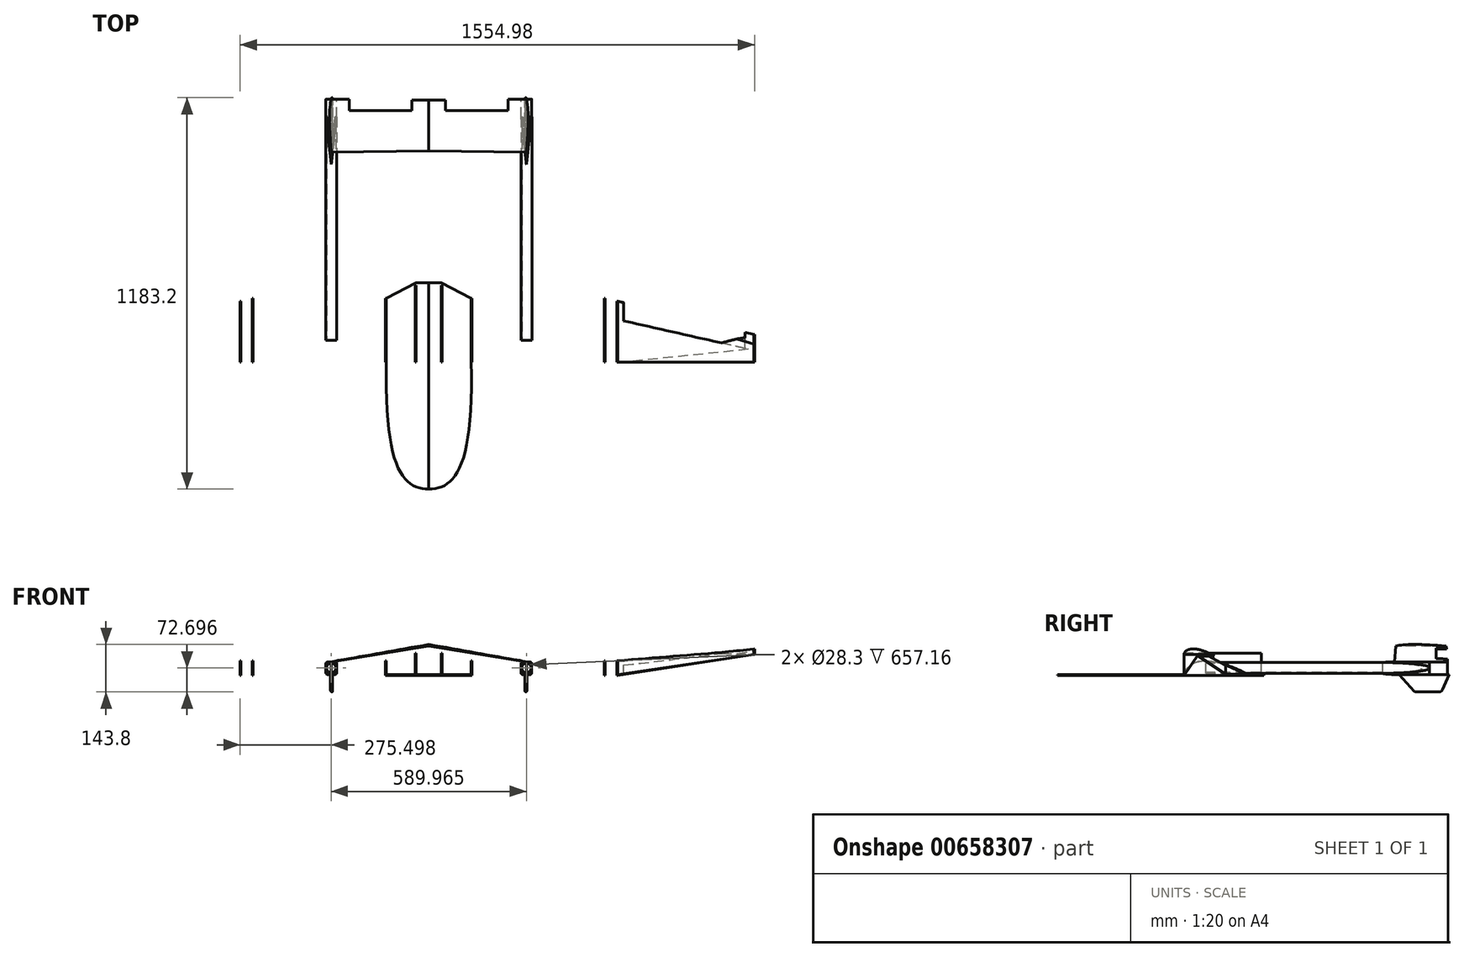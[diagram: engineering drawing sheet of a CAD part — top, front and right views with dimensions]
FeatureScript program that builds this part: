
annotation { "Feature Type Name" : "Feature", "Feature Type Description" : "" }
export const myFeature = defineFeature(function(context is Context, id is Id, definition is map)
    precondition{}
    {
        {
            var Q0;
            Q0=qCreatedBy(makeId("Top.planeOp"),FACE);
            var sketch = newSketch(context, id + "F0", { "sketchPlane" : qUnion([Q0])});
            skLineSegment(sketch, "E0", {"start": v(0, 0) * mm, "end": v(0, -382.94) * mm});
            skFitSpline(sketch, "E1", {"points": [v(0, -382.94) * mm, v(128.36, 0) * mm], "startDerivative": vector(233.61, 0) * mm, "endDerivative": vector(-19.39, 965.68) * mm});
            skLineSegment(sketch, "E2", {"start": v(128.36, 0) * mm, "end": v(1020.01, 0) * mm});
            skLineSegment(sketch, "E3", {"start": v(1020.01, 0) * mm, "end": v(1020.01, 80.94) * mm});
            skLineSegment(sketch, "E4", {"start": v(1020.01, 80.94) * mm, "end": v(531.82, 193.85) * mm});
            skLineSegment(sketch, "E5", {"start": v(531.82, 193.85) * mm, "end": v(128.36, 193.85) * mm});
            skLineSegment(sketch, "E6", {"start": v(0, 240.34) * mm, "end": v(0, 0) * mm});
            skLineSegment(sketch, "E7", {"start": v(128.36, 0) * mm, "end": v(128.36, 193.85) * mm});
            skLineSegment(sketch, "E8", {"start": v(531.82, 193.85) * mm, "end": v(531.82, 0) * mm});
            skLineSegment(sketch, "E9", {"start": v(568.3, 185.41) * mm, "end": v(568.3, 130.1) * mm});
            skLineSegment(sketch, "E10", {"start": v(568.3, 130.1) * mm, "end": v(981.05, 34.63) * mm});
            skLineSegment(sketch, "E11", {"start": v(981.05, 34.63) * mm, "end": v(981.05, 89.95) * mm});
            skLineSegment(sketch, "E12", {"start": v(0, 240.34) * mm, "end": v(38.04, 240.34) * mm});
            skLineSegment(sketch, "E13", {"start": v(38.04, 240.34) * mm, "end": v(128.36, 193.85) * mm});
            skSolve(sketch);
        }
        {
            var Q0;
            Q0=qCreatedBy(makeId("Right.planeOp"),FACE);
            var sketch = newSketch(context, id + "F1", { "sketchPlane" : qUnion([Q0])});
            skFitSpline(sketch, "E14", {"points": [v(-382.75, 0) * mm, v(0, 95.17) * mm], "startDerivative": vector(82.74, 188.65) * mm, "endDerivative": vector(471.18, 30.82) * mm});
            skLineSegment(sketch, "E15", {"start": v(-382.75, 0) * mm, "end": v(240.8, 0) * mm});
            skLineSegment(sketch, "E16", {"start": v(240.8, 0) * mm, "end": v(240.8, 95.17) * mm});
            skLineSegment(sketch, "E17", {"start": v(240.8, 95.17) * mm, "end": v(0, 95.17) * mm});
            skSolve(sketch);
        }
        {
            var Q0;
            Q0=sQuery(id+"F0.wireOp",EDGE,"E1");
            var Q1;
            Q1=sQuery(id+"F1.wireOp",EDGE,"E14");
            loft(context, id + "F2", {"bodyType" : ToolBodyType.SURFACE, "wireProfilesArray" : [{ "wireProfileEntities" : qUnion([Q0]) }, { "wireProfileEntities" : qUnion([Q1]) }]});
        }
        {
            var Q0;
            Q0=makeQuery(id+"F0.imprint","IMPRINT",FACE,{"disambiguationData":[TD([[makeQuery(id+"F0.imprint","IMPRINT",EDGE,{"derivedFrom":sQuery(id+"F0.wireOp",EDGE,"E0")}),1.0]])]});
            extrude(context, id + "F3", {"entities" : qUnion([Q0]), "oppositeDirection" : true, "depth" : 2.54 * mm, "offsetDistance" : 25.4 * mm});
        }
        {
            var Q0;
            Q0=makeQuery(id+"F3.opExtrude","SWEPT_FACE",FACE,{"disambiguationData":[OSD([sQuery(id+"F0.wireOp",EDGE,"E7")])]});
            var sketch = newSketch(context, id + "F4", { "sketchPlane" : qUnion([Q0])});
            skFitSpline(sketch, "E18", {"points": [v(0, 0) * mm, v(193.85, 0) * mm], "startDerivative": vector(91.66, 269.25) * mm, "endDerivative": vector(55.9, -26.92) * mm});
            skLineSegment(sketch, "E19", {"start": v(0, 0) * mm, "end": v(0, -2.54) * mm});
            skLineSegment(sketch, "E20", {"start": v(0, -2.54) * mm, "end": v(193.85, -2.54) * mm});
            skLineSegment(sketch, "E21", {"start": v(193.85, -2.54) * mm, "end": v(193.85, 0) * mm});
            skSolve(sketch);
        }
        {
            var Q0;
            Q0 = qSketchRegion(id + "F4", true);
            extrude(context, id + "F5", {"entities" : qUnion([Q0]), "operationType" : NewBodyOperationType.ADD, "depth" : 2.54 * mm, "offsetDistance" : 25.4 * mm});
        }
        {
            var Q0;
            Q0=qCreatedBy(makeId("Right.planeOp"),FACE);
            cPlane(context, id + "F6", {"entities" : qUnion([Q0]), "cplaneType" : CPlaneType.OFFSET, "offset" : 40.64 * mm, "width" : 152.4 * mm, "height" : 152.4 * mm});
        }
        {
            var Q0;
            Q0=qCreatedBy(id+"F6.planeOp",FACE);
            var sketch = newSketch(context, id + "F7", { "sketchPlane" : qUnion([Q0])});
            skLineSegment(sketch, "E22", {"start": v(0, 65.06) * mm, "end": v(0, 0) * mm});
            skLineSegment(sketch, "E23", {"start": v(0, 0) * mm, "end": v(233.41, 0) * mm});
            skLineSegment(sketch, "E24", {"start": v(233.41, 0) * mm, "end": v(233.41, 65.06) * mm});
            skLineSegment(sketch, "E25", {"start": v(233.41, 65.06) * mm, "end": v(0, 65.06) * mm});
            skSolve(sketch);
        }
        {
            var Q0;
            Q0 = qSketchRegion(id + "F7", true);
            extrude(context, id + "F8", {"entities" : qUnion([Q0]), "operationType" : NewBodyOperationType.ADD, "oppositeDirection" : true, "depth" : 2.54 * mm, "offsetDistance" : 25.4 * mm});
        }
        {
            var Q0;
            Q0=makeQuery(id+"F8.opExtrude","CAP_EDGE",EDGE,{"disambiguationData":[OSD([sQuery(id+"F7.wireOp",EDGE,"E25")])],"isStart":true});
            var Q1;
            Q1=sQuery(id+"F1.wireOp",EDGE,"E17");
            loft(context, id + "F9", {"bodyType" : ToolBodyType.SURFACE, "wireProfilesArray" : [{ "wireProfileEntities" : qUnion([Q0]) }, { "wireProfileEntities" : qUnion([Q1]) }]});
        }
        {
            var Q0;
            Q0=makeQuery(id+"F9.opLoft","SWEPT_BODY",BODY,{"disambiguationData":[OSD([sQuery(id+"F1.wireOp",EDGE,"E17"),sQuery(id+"F7.wireOp",EDGE,"E25")])]});
            var Q1;
            Q1=makeQuery(id+"F9.opLoft","MID_CAP_EDGE",EDGE,{"disambiguationData":[OSD([sQuery(id+"F7.wireOp",EDGE,"E22"),sQuery(id+"F7.wireOp",EDGE,"E24"),sQuery(id+"F7.wireOp",EDGE,"E25")])],"capPos":0.0});
            var Q2;
            Q2=makeQuery(id+"F5.opExtrude","CAP_EDGE",EDGE,{"disambiguationData":[OSD([sQuery(id+"F4.wireOp",EDGE,"E18")])],"isStart":true});
            loft(context, id + "F10", {"bodyType" : ToolBodyType.SURFACE, "sheetProfilesArray" : [{ "sheetProfileEntities" : qUnion([Q0]) }], "wireProfilesArray" : [{ "wireProfileEntities" : qUnion([Q1]) }, { "wireProfileEntities" : qUnion([Q2]) }]});
        }
        {
            var Q0;
            Q0=qCreatedBy(makeId("Right.planeOp"),FACE);
            cPlane(context, id + "F11", {"entities" : qUnion([Q0]), "cplaneType" : CPlaneType.OFFSET, "offset" : 530.86 * mm, "width" : 152.4 * mm, "height" : 152.4 * mm});
        }
        {
            var Q0;
            Q0=qCreatedBy(id+"F11.planeOp",FACE);
            var sketch = newSketch(context, id + "F12", { "sketchPlane" : qUnion([Q0])});
            skFitSpline(sketch, "E26", {"points": [v(0, 0) * mm, v(193.85, 0) * mm], "startDerivative": vector(87.77, 268.75) * mm, "endDerivative": vector(39.83, -20.5) * mm});
            skLineSegment(sketch, "E27", {"start": v(193.85, 0) * mm, "end": v(193.85, -2.56) * mm});
            skLineSegment(sketch, "E28", {"start": v(0, 0) * mm, "end": v(0, -2.54) * mm});
            skLineSegment(sketch, "E29", {"start": v(0, -2.54) * mm, "end": v(193.85, -2.56) * mm});
            skSolve(sketch);
        }
        {
            var Q0;
            Q0 = qSketchRegion(id + "F12", true);
            extrude(context, id + "F13", {"entities" : qUnion([Q0]), "depth" : 2.54 * mm, "offsetDistance" : 25.4 * mm});
        }
        {
            var Q0;
            Q0=makeQuery(id+"F5.opExtrude","CAP_EDGE",EDGE,{"disambiguationData":[OSD([sQuery(id+"F4.wireOp",EDGE,"E18")])],"isStart":false});
            var Q1;
            Q1=makeQuery(id+"F13.opExtrude","CAP_EDGE",EDGE,{"disambiguationData":[OSD([sQuery(id+"F12.wireOp",EDGE,"E26")])],"isStart":true});
            loft(context, id + "F14", {"bodyType" : ToolBodyType.SURFACE, "wireProfilesArray" : [{ "wireProfileEntities" : qUnion([Q0]) }, { "wireProfileEntities" : qUnion([Q1]) }]});
        }
        {
            var Q0;
            Q0=sQuery(id+"F0.wireOp",EDGE,"E7");
            var Q1;
            Q1=makeQuery(id+"F13.opExtrude","CAP_EDGE",EDGE,{"disambiguationData":[OSD([sQuery(id+"F12.wireOp",EDGE,"E29")])],"isStart":true});
            loft(context, id + "F15", {"bodyType" : ToolBodyType.SURFACE, "wireProfilesArray" : [{ "wireProfileEntities" : qUnion([Q0]) }, { "wireProfileEntities" : qUnion([Q1]) }]});
        }
        {
            var Q0;
            Q0=qCreatedBy(id+"F11.planeOp",FACE);
            cPlane(context, id + "F16", {"entities" : qUnion([Q0]), "cplaneType" : CPlaneType.OFFSET, "offset" : 37.08 * mm, "width" : 152.4 * mm, "height" : 152.4 * mm});
        }
        {
            var Q0;
            Q0=qCreatedBy(id+"F16.planeOp",FACE);
            var sketch = newSketch(context, id + "F17", { "sketchPlane" : qUnion([Q0])});
            skFitSpline(sketch, "E30", {"points": [v(0, 0) * mm, v(185.26, 0) * mm], "startDerivative": vector(98.18, 281.16) * mm, "endDerivative": vector(14.13, 0) * mm});
            skLineSegment(sketch, "E31", {"start": v(0, 0) * mm, "end": v(0, -2.42) * mm});
            skLineSegment(sketch, "E32", {"start": v(0, -2.42) * mm, "end": v(185.14, -2.42) * mm});
            skLineSegment(sketch, "E33", {"start": v(185.14, -2.42) * mm, "end": v(185.26, 0) * mm});
            skLineSegment(sketch, "E34", {"start": v(131.84, -2.42) * mm, "end": v(131.84, 25.26) * mm});
            skSolve(sketch);
        }
        {
            var Q0;
            Q0 = qSketchRegion(id + "F17", true);
            extrude(context, id + "F18", {"entities" : qUnion([Q0]), "depth" : 2.54 * mm, "offsetDistance" : 25.4 * mm});
        }
        {
            var Q0;
            Q0=makeQuery(id+"F13.opExtrude","CAP_FACE",FACE,{"disambiguationData":[OSD([sQuery(id+"F12.wireOp",EDGE,"E26"),sQuery(id+"F12.wireOp",EDGE,"E27"),sQuery(id+"F12.wireOp",EDGE,"E28"),sQuery(id+"F12.wireOp",EDGE,"E29")])],"isStart":false});
            var Q1;
            Q1=makeQuery(id+"F13.opExtrude","CAP_EDGE",EDGE,{"disambiguationData":[OSD([sQuery(id+"F12.wireOp",EDGE,"E26")])],"isStart":false});
            var Q2;
            Q2=makeQuery(id+"F18.opExtrude","CAP_EDGE",EDGE,{"disambiguationData":[OSD([sQuery(id+"F17.wireOp",EDGE,"E30")])],"isStart":true});
            loft(context, id + "F19", {"bodyType" : ToolBodyType.SURFACE, "sheetProfilesArray" : [{ "sheetProfileEntities" : qUnion([Q0]) }], "wireProfilesArray" : [{ "wireProfileEntities" : qUnion([Q1]) }, { "wireProfileEntities" : qUnion([Q2]) }]});
        }
        {
            var Q0;
            Q0=makeQuery(id+"F18.opExtrude","CAP_EDGE",EDGE,{"disambiguationData":[OSD([sQuery(id+"F17.wireOp",EDGE,"E32")])],"isStart":true});
            var Q1;
            Q1=makeQuery(id+"F13.opExtrude","CAP_EDGE",EDGE,{"disambiguationData":[OSD([sQuery(id+"F12.wireOp",EDGE,"E29")])],"isStart":false});
            loft(context, id + "F20", {"bodyType" : ToolBodyType.SURFACE, "wireProfilesArray" : [{ "wireProfileEntities" : qUnion([Q0]) }, { "wireProfileEntities" : qUnion([Q1]) }]});
        }
        {
            var Q0;
            Q0=qCreatedBy(id+"F16.planeOp",FACE);
            cPlane(context, id + "F21", {"entities" : qUnion([Q0]), "cplaneType" : CPlaneType.OFFSET, "offset" : 414.02 * mm, "width" : 152.4 * mm, "height" : 152.4 * mm});
        }
        {
            var Q0;
            Q0=qCreatedBy(id+"F21.planeOp",FACE);
            var sketch = newSketch(context, id + "F22", { "sketchPlane" : qUnion([Q0])});
            skLineSegment(sketch, "E35", {"start": v(0, 60.1) * mm, "end": v(84.44, 60.1) * mm});
            skLineSegment(sketch, "E36", {"start": v(27.71, 60.1) * mm, "end": v(27.71, 77.24) * mm});
            skFitSpline(sketch, "E37", {"points": [v(0, 60.1) * mm, v(27.71, 77.24) * mm, v(84.44, 60.1) * mm], "startDerivative": vector(0, 93.67) * mm, "endDerivative": vector(108.46, -49.98) * mm});
            skSolve(sketch);
        }
        {
            var Q0;
            Q0 = qSketchRegion(id + "F22", true);
            extrude(context, id + "F23", {"entities" : qUnion([Q0]), "depth" : 2.54 * mm, "offsetDistance" : 25.4 * mm});
        }
        {
            var Q0;
            Q0=makeQuery(id+"F18.opExtrude","CAP_FACE",FACE,{"disambiguationData":[OSD([sQuery(id+"F17.wireOp",EDGE,"E30"),sQuery(id+"F17.wireOp",EDGE,"E31"),sQuery(id+"F17.wireOp",EDGE,"E32"),sQuery(id+"F17.wireOp",EDGE,"E33")])],"isStart":false});
            var Q1;
            Q1=makeQuery(id+"F23.opExtrude","CAP_FACE",FACE,{"disambiguationData":[OSD([sQuery(id+"F22.wireOp",EDGE,"c30c6b66-d443-4e39-8451-170bddd20a5f"),sQuery(id+"F22.wireOp",EDGE,"S6skx1oO-r8w3-M7RH-89HN-Rbgwb9d3iRie"),sQuery(id+"F22.wireOp",EDGE,"E35"),sQuery(id+"F22.wireOp",EDGE,"XofBSCwt-zFux-jAat-FpLT-tnajAGSUlYNw")])],"isStart":true});
            loft(context, id + "F24", {"sheetProfilesArray" : [{ "sheetProfileEntities" : qUnion([Q0]) }, { "sheetProfileEntities" : qUnion([Q1]) }]});
        }
        {
            var Q0;
            Q0=qCreatedBy(makeId("Top.planeOp"),FACE);
            var sketch = newSketch(context, id + "F25", { "sketchPlane" : qUnion([Q0])});
            skLineSegment(sketch, "E38", {"start": v(589.31, 183.72) * mm, "end": v(589.31, 125.4) * mm});
            skLineSegment(sketch, "E39", {"start": v(589.31, 125.4) * mm, "end": v(956.1, 42.53) * mm});
            skLineSegment(sketch, "E40", {"start": v(956.1, 42.53) * mm, "end": v(956.1, 97.78) * mm});
            skLineSegment(sketch, "E41", {"start": v(956.1, 97.78) * mm, "end": v(589.31, 183.72) * mm});
            skSolve(sketch);
        }
        {
            var Q0;
            Q0 = qSketchRegion(id + "F25", true);
            extrude(context, id + "F26", {"entities" : qUnion([Q0]), "operationType" : NewBodyOperationType.REMOVE, "oppositeDirection" : true, "depth" : 25.4 * mm, "offsetDistance" : 25.4 * mm, "hasSecondDirection" : true, "secondDirectionOppositeDirection" : false, "secondDirectionDepth" : 63.5 * mm});
        }
        {
            var Q0;
            Q0=qCreatedBy(makeId("Front.planeOp"),FACE);
            cPlane(context, id + "F27", {"entities" : qUnion([Q0]), "cplaneType" : CPlaneType.OFFSET, "offset" : 66.04 * mm, "oppositeDirection" : true, "width" : 152.4 * mm, "height" : 152.4 * mm});
        }
        {
            var Q0;
            Q0=qCreatedBy(id+"F27.planeOp",FACE);
            var sketch = newSketch(context, id + "F28", { "sketchPlane" : qUnion([Q0])});
            skCircle(sketch, "E42", {"center": v(294.98, 19.94) * mm, "radius": 16.32 * mm});
            skCircle(sketch, "E43", {"center": v(294.98, 19.94) * mm, "radius": 14.15 * mm});
            skSolve(sketch);
        }
        {
            var Q0;
            Q0 = qSketchRegion(id + "F28", true);
            extrude(context, id + "F29", {"entities" : qUnion([Q0]), "operationType" : NewBodyOperationType.ADD, "oppositeDirection" : true, "depth" : 675.64 * mm, "offsetDistance" : 25.4 * mm});
        }
        {
            var Q0;
            Q0=qCreatedBy(makeId("Top.planeOp"),FACE);
            var sketch = newSketch(context, id + "F30", { "sketchPlane" : qUnion([Q0])});
            skLineSegment(sketch, "E44", {"start": v(294.86, 741.49) * mm, "end": v(294.86, 598.34) * mm});
            skFitSpline(sketch, "E45", {"points": [v(294.86, 598.34) * mm, v(311.17, 741.68) * mm], "startDerivative": vector(15.62, 145.99) * mm, "endDerivative": vector(15.62, 145.99) * mm});
            skLineSegment(sketch, "E46", {"start": v(311.17, 741.68) * mm, "end": v(311.17, 795.98) * mm});
            skLineSegment(sketch, "E47", {"start": v(311.17, 795.98) * mm, "end": v(294.86, 795.98) * mm});
            skLineSegment(sketch, "E48", {"start": v(294.86, 795.98) * mm, "end": v(294.86, 741.49) * mm});
            skLineSegment(sketch, "E49.MirrorCS", {"start": v(278.55, 795.98) * mm, "end": v(294.86, 795.98) * mm});
            skLineSegment(sketch, "E50.MirrorCS", {"start": v(278.55, 741.68) * mm, "end": v(278.55, 795.98) * mm});
            skFitSpline(sketch, "E51.MirrorCS", {"points": [v(294.86, 598.34) * mm, v(278.55, 741.68) * mm], "startDerivative": vector(-15.62, 145.99) * mm, "endDerivative": vector(-15.62, 145.99) * mm});
            skSolve(sketch);
        }
        {
            var Q0;
            Q0 = qSketchRegion(id + "F30", true);
            extrude(context, id + "F31", {"entities" : qUnion([Q0]), "operationType" : NewBodyOperationType.ADD, "depth" : 37.85 * mm, "offsetDistance" : 25.4 * mm});
        }
        {
            var Q0;
            Q0=makeQuery(id+"F31.opExtrude","CAP_EDGE",EDGE,{"disambiguationData":[OSD([sQuery(id+"F30.wireOp",EDGE,"E45")])],"isStart":false});
            var Q1;
            Q1=makeQuery(id+"F31.opExtrude","CAP_EDGE",EDGE,{"disambiguationData":[OSD([sQuery(id+"F30.wireOp",EDGE,"E46")])],"isStart":false});
            var Q2;
            Q2=makeQuery(id+"F31.opExtrude","CAP_EDGE",EDGE,{"disambiguationData":[OSD([sQuery(id+"F30.wireOp",EDGE,"E45")])],"isStart":true});
            var Q3;
            Q3=makeQuery(id+"F31.opExtrude","CAP_EDGE",EDGE,{"disambiguationData":[OSD([sQuery(id+"F30.wireOp",EDGE,"E46")])],"isStart":true});
            var Q4;
            Q4=makeQuery(id+"F31.opExtrude","CAP_EDGE",EDGE,{"disambiguationData":[OSD([sQuery(id+"F30.wireOp",EDGE,"E50.MirrorCS")])],"isStart":false});
            var Q5;
            Q5=makeQuery(id+"F31.opExtrude","CAP_EDGE",EDGE,{"disambiguationData":[OSD([sQuery(id+"F30.wireOp",EDGE,"E51.MirrorCS")])],"isStart":false});
            var Q6;
            Q6=makeQuery(id+"F31.opExtrude","CAP_EDGE",EDGE,{"disambiguationData":[OSD([sQuery(id+"F30.wireOp",EDGE,"E50.MirrorCS")])],"isStart":true});
            var Q7;
            Q7=makeQuery(id+"F31.opExtrude","CAP_EDGE",EDGE,{"disambiguationData":[OSD([sQuery(id+"F30.wireOp",EDGE,"E51.MirrorCS")])],"isStart":true});
            fillet(context, id + "F32", {"entities" : qUnion([Q0, Q1, Q2, Q3, Q4, Q5, Q6, Q7]), "radius" : 5.08 * mm, "tangentPropagation" : true, "allowEdgeOverflow" : false});
        }
        {
            var Q0;
            Q0=sQuery(id+"F0.wireOp",EDGE,"E2");
            var Q1;
            Q1=makeQuery(id+"F15.opLoft","SWEPT_EDGE",EDGE,{"disambiguationData":[OSD([sQuery(id+"F0.wireOp",VERTEX,"E7.start"),sQuery(id+"F12.wireOp",EDGE,"E28"),sQuery(id+"F12.wireOp",EDGE,"E29")])]});
            loft(context, id + "F33", {"bodyType" : ToolBodyType.SURFACE, "wireProfilesArray" : [{ "wireProfileEntities" : qUnion([Q0]) }, { "wireProfileEntities" : qUnion([Q1]) }]});
        }
        {
            var Q0;
            Q0=makeQuery(id+"F10.opLoft","SWEPT_EDGE",EDGE,{"disambiguationData":[OSD([sQuery(id+"F0.wireOp",EDGE,"E5"),sQuery(id+"F0.wireOp",EDGE,"E7"),sQuery(id+"F0.wireOp",EDGE,"E13"),sQuery(id+"F4.wireOp",EDGE,"E18"),sQuery(id+"F4.wireOp",EDGE,"E21"),sQuery(id+"F7.wireOp",EDGE,"E24"),sQuery(id+"F7.wireOp",EDGE,"E25")])]});
            var Q1;
            Q1=sQuery(id+"F0.wireOp",EDGE,"E13");
            loft(context, id + "F34", {"bodyType" : ToolBodyType.SURFACE, "wireProfilesArray" : [{ "wireProfileEntities" : qUnion([Q0]) }, { "wireProfileEntities" : qUnion([Q1]) }]});
        }
        {
            var Q0;
            Q0=qCreatedBy(makeId("Right.planeOp"),FACE);
            cPlane(context, id + "F35", {"entities" : qUnion([Q0]), "cplaneType" : CPlaneType.OFFSET, "offset" : 293.88 * mm, "width" : 152.4 * mm, "height" : 152.4 * mm});
        }
        {
            var Q0;
            Q0=qCreatedBy(id+"F35.planeOp",FACE);
            var sketch = newSketch(context, id + "F36", { "sketchPlane" : qUnion([Q0])});
            skLineSegment(sketch, "E52", {"start": v(800.26, 0) * mm, "end": v(780.86, -45.8) * mm});
            skLineSegment(sketch, "E53", {"start": v(770.33, -52.76) * mm, "end": v(700.76, -52.76) * mm});
            skLineSegment(sketch, "E54", {"start": v(696.08, -50.71) * mm, "end": v(649.46, 0) * mm});
            skLineSegment(sketch, "E55", {"start": v(649.46, 0) * mm, "end": v(800.26, 0) * mm});
            skPoint(sketch, "E56.visualSharp", {"position": v(697.97, -52.76) * mm});
            skArc(sketch, "E56.filletArc", {"start": v(696.08, -50.71) * mm, "mid": v(698.2, -52.23) * mm, "end": v(700.76, -52.76) * mm});
            skPoint(sketch, "E57.visualSharp", {"position": v(777.9, -52.76) * mm});
            skArc(sketch, "E57.filletArc", {"start": v(770.33, -52.76) * mm, "mid": v(776.65, -50.86) * mm, "end": v(780.86, -45.8) * mm});
            skSolve(sketch);
        }
        {
            var Q0;
            Q0 = qSketchRegion(id + "F36", true);
            extrude(context, id + "F37", {"entities" : qUnion([Q0]), "operationType" : NewBodyOperationType.ADD, "endBound" : BoundingType.SYMMETRIC, "depth" : 6.35 * mm, "offsetDistance" : 25.4 * mm});
        }
        {
            var Q0;
            Q0=makeQuery(id+"F37.opExtrude","CAP_EDGE",EDGE,{"disambiguationData":[OSD([sQuery(id+"F36.wireOp",EDGE,"E54")])],"isStart":false});
            fillet(context, id + "F38", {"entities" : qUnion([Q0]), "radius" : 5.08 * mm, "tangentPropagation" : true, "allowEdgeOverflow" : false});
        }
        {
            var Q0;
            Q0=makeQuery(id+"F37.opExtrude","CAP_EDGE",EDGE,{"disambiguationData":[OSD([sQuery(id+"F36.wireOp",EDGE,"E54")])],"isStart":true});
            fillet(context, id + "F39", {"entities" : qUnion([Q0]), "radius" : 5.08 * mm, "tangentPropagation" : true, "allowEdgeOverflow" : false});
        }
        {
            var Q0;
            Q0=makeQuery(id+"F31.opExtrude","CAP_FACE",FACE,{"disambiguationData":[OSD([sQuery(id+"F30.wireOp",EDGE,"E45"),sQuery(id+"F30.wireOp",EDGE,"E46"),sQuery(id+"F30.wireOp",EDGE,"E47"),sQuery(id+"F30.wireOp",EDGE,"E49.MirrorCS"),sQuery(id+"F30.wireOp",EDGE,"E50.MirrorCS"),sQuery(id+"F30.wireOp",EDGE,"E51.MirrorCS")])],"isStart":false});
            var sketch = newSketch(context, id + "F40", { "sketchPlane" : qUnion([Q0])});
            skLineSegment(sketch, "E58", {"start": v(294.88, 635.6) * mm, "end": v(294.88, 795.98) * mm});
            skFitSpline(sketch, "E59", {"points": [v(294.88, 635.6) * mm, v(294.88, 795.98) * mm], "startDerivative": vector(5.18, 56.04) * mm, "endDerivative": vector(-33.62, 106.5) * mm});
            skSolve(sketch);
        }
        {
            var Q0;
            Q0=makeQuery(id+"F40.imprint","IMPRINT",FACE,{"disambiguationData":[TD([[makeQuery(id+"F40.imprint","IMPRINT",EDGE,{"derivedFrom":sQuery(id+"F40.wireOp",EDGE,"E58")}),-1.0]])]});
            var sketch = newSketch(context, id + "F41", { "sketchPlane" : qUnion([Q0])});
            skSolve(sketch);
        }
        {
            var Q0;
            Q0=qCreatedBy(makeId("Right.planeOp"),FACE);
            var sketch = newSketch(context, id + "F42", { "sketchPlane" : qUnion([Q0])});
            skLineSegment(sketch, "E60", {"start": v(792.55, 85.65) * mm, "end": v(639.4, 85.65) * mm});
            skFitSpline(sketch, "E61", {"points": [v(792.55, 85.65) * mm, v(639.4, 85.65) * mm], "startDerivative": vector(-56.04, 5.21) * mm, "endDerivative": vector(-106.5, -33.62) * mm});
            skSolve(sketch);
        }
        {
            var Q1;
            Q1=makeQuery(id+"F42.imprint","IMPRINT",FACE,{"disambiguationData":[TD([[makeQuery(id+"F42.imprint","IMPRINT",EDGE,{"derivedFrom":sQuery(id+"F42.wireOp",EDGE,"E60")}),-1.0]])]});
            var Q2;
            Q2=makeQuery(id+"F41.imprint","IMPRINT",FACE,{"disambiguationData":[TD([[makeQuery(id+"F41.imprint","IMPRINT",EDGE,{"derivedFrom":makeQuery(id+"F40.imprint","IMPRINT",EDGE,{"derivedFrom":sQuery(id+"F40.wireOp",EDGE,"E58")})}),-1.0]])]});
            loft(context, id + "F43", {"operationType" : NewBodyOperationType.ADD, "sheetProfilesArray" : [{ "sheetProfileEntities" : qUnion([Q1]) }, { "sheetProfileEntities" : qUnion([Q2]) }]});
        }
        {
            var Q0;
            Q0=qCreatedBy(makeId("Top.planeOp"),FACE);
            var sketch = newSketch(context, id + "F44", { "sketchPlane" : qUnion([Q0])});
            skLineSegment(sketch, "E62.bottom", {"start": v(239.97, 822.85) * mm, "end": v(50.83, 822.85) * mm});
            skLineSegment(sketch, "E62.top", {"start": v(239.97, 761.32) * mm, "end": v(50.83, 761.32) * mm});
            skLineSegment(sketch, "E62.left", {"start": v(239.97, 822.85) * mm, "end": v(239.97, 761.32) * mm});
            skLineSegment(sketch, "E62.right", {"start": v(50.83, 822.85) * mm, "end": v(50.83, 761.32) * mm});
            skSolve(sketch);
        }
        {
            var Q0;
            Q0=makeQuery(id+"F44.imprint","IMPRINT",FACE,{"disambiguationData":[TD([[makeQuery(id+"F44.imprint","IMPRINT",EDGE,{"derivedFrom":sQuery(id+"F44.wireOp",EDGE,"E62.bottom")}),1.0]])]});
            extrude(context, id + "F45", {"entities" : qUnion([Q0]), "operationType" : NewBodyOperationType.REMOVE, "depth" : 335.28 * mm, "offsetDistance" : 25.4 * mm});
        }
        {
            var Q0;
            Q0=makeQuery(id+"F2.opLoft","SWEPT_BODY",BODY,{"disambiguationData":[OSD([sQuery(id+"F0.wireOp",EDGE,"E1"),sQuery(id+"F1.wireOp",EDGE,"E14")])]});
            var Q1;
            Q1=makeQuery(id+"F14.opLoft","SWEPT_BODY",BODY,{"disambiguationData":[OSD([sQuery(id+"F4.wireOp",EDGE,"E18"),sQuery(id+"F12.wireOp",EDGE,"E26")])]});
            var Q2;
            Q2=makeQuery(id+"F18.opExtrude","SWEPT_BODY",BODY,{"disambiguationData":[OSD([sQuery(id+"F17.wireOp",EDGE,"E30"),sQuery(id+"F17.wireOp",EDGE,"E31"),sQuery(id+"F17.wireOp",EDGE,"E32"),sQuery(id+"F17.wireOp",EDGE,"E33")])]});
            var Q3;
            Q3=makeQuery(id+"F29.opExtrude","SWEPT_BODY",BODY,{"disambiguationData":[OSD([sQuery(id+"F28.wireOp",EDGE,"E42"),sQuery(id+"F28.wireOp",EDGE,"E43")])]});
            var Q4;
            Q4=makeQuery(id+"F3.opExtrude","SWEPT_BODY",BODY,{"disambiguationData":[OSD([sQuery(id+"F0.wireOp",EDGE,"E0"),sQuery(id+"F0.wireOp",EDGE,"E1"),sQuery(id+"F0.wireOp",EDGE,"E6"),sQuery(id+"F0.wireOp",EDGE,"E7"),sQuery(id+"F0.wireOp",EDGE,"E12"),sQuery(id+"F0.wireOp",EDGE,"E13")])]});
            var Q5;
            Q5=makeQuery(id+"F15.opLoft","SWEPT_BODY",BODY,{"disambiguationData":[OSD([sQuery(id+"F0.wireOp",EDGE,"E7"),sQuery(id+"F12.wireOp",EDGE,"E29")])]});
            var Q6;
            Q6=makeQuery(id+"F19.opLoft","SWEPT_BODY",BODY,{"disambiguationData":[OSD([sQuery(id+"F12.wireOp",EDGE,"E26"),sQuery(id+"F17.wireOp",EDGE,"E30")])]});
            var Q7;
            Q7=makeQuery(id+"F33.opLoft","SWEPT_BODY",BODY,{"disambiguationData":[OSD([sQuery(id+"F0.wireOp",VERTEX,"E7.start"),sQuery(id+"F0.wireOp",EDGE,"E2"),sQuery(id+"F12.wireOp",EDGE,"E28"),sQuery(id+"F12.wireOp",EDGE,"E29")])]});
            var Q8;
            Q8=makeQuery(id+"F9.opLoft","SWEPT_BODY",BODY,{"disambiguationData":[OSD([sQuery(id+"F1.wireOp",EDGE,"E17"),sQuery(id+"F7.wireOp",EDGE,"E25")])]});
            var Q9;
            Q9=makeQuery(id+"F13.opExtrude","SWEPT_BODY",BODY,{"disambiguationData":[OSD([sQuery(id+"F12.wireOp",EDGE,"E26"),sQuery(id+"F12.wireOp",EDGE,"E27"),sQuery(id+"F12.wireOp",EDGE,"E28"),sQuery(id+"F12.wireOp",EDGE,"E29")])]});
            var Q10;
            Q10=makeQuery(id+"F10.opLoft","SWEPT_BODY",BODY,{"disambiguationData":[OSD([sQuery(id+"F4.wireOp",EDGE,"E18"),sQuery(id+"F7.wireOp",EDGE,"E22"),sQuery(id+"F7.wireOp",EDGE,"E24"),sQuery(id+"F7.wireOp",EDGE,"E25")])]});
            var Q11;
            Q11=makeQuery(id+"F20.opLoft","SWEPT_BODY",BODY,{"disambiguationData":[OSD([sQuery(id+"F12.wireOp",EDGE,"E29"),sQuery(id+"F17.wireOp",EDGE,"E32")])]});
            var Q12;
            Q12=makeQuery(id+"F34.opLoft","SWEPT_BODY",BODY,{"disambiguationData":[OSD([sQuery(id+"F0.wireOp",EDGE,"E5"),sQuery(id+"F0.wireOp",EDGE,"E7"),sQuery(id+"F0.wireOp",EDGE,"E13"),sQuery(id+"F4.wireOp",EDGE,"E18"),sQuery(id+"F4.wireOp",EDGE,"E21"),sQuery(id+"F7.wireOp",EDGE,"E24"),sQuery(id+"F7.wireOp",EDGE,"E25")])]});
            var Q13;
            Q13=qCreatedBy(makeId("Right.planeOp"),FACE);
            mirror(context, id + "F46", {"entities" : qUnion([Q0, Q1, Q2, Q3, Q4, Q5, Q6, Q7, Q8, Q9, Q10, Q11, Q12]), "mirrorPlane" : qUnion([Q13])});
        }
    });
